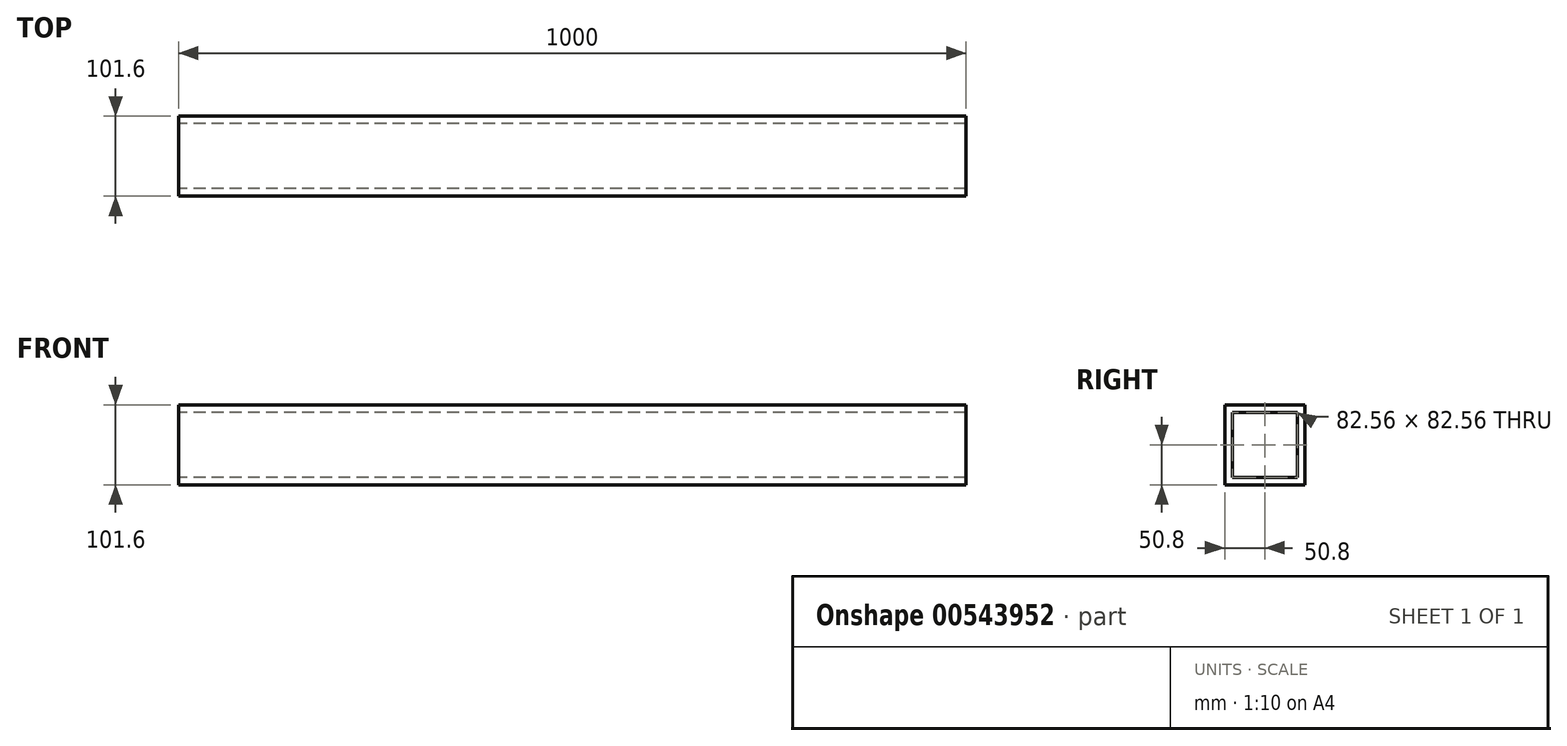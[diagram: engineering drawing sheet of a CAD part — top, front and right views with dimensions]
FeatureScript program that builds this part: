
annotation { "Feature Type Name" : "Feature", "Feature Type Description" : "" }
export const myFeature = defineFeature(function(context is Context, id is Id, definition is map)
    precondition{}
    {
        {
            var Q0;
            Q0=qCreatedBy(makeId("Right.planeOp"),FACE);
            var sketch = newSketch(context, id + "F0", { "sketchPlane" : qUnion([Q0])});
            skLineSegment(sketch, "E0.bottom", {"start": v(-50.8, 50.8) * mm, "end": v(50.8, 50.8) * mm});
            skLineSegment(sketch, "E0.top", {"start": v(-50.8, -50.8) * mm, "end": v(50.8, -50.8) * mm});
            skLineSegment(sketch, "E0.left", {"start": v(-50.8, 50.8) * mm, "end": v(-50.8, -50.8) * mm});
            skLineSegment(sketch, "E0.right", {"start": v(50.8, 50.8) * mm, "end": v(50.8, -50.8) * mm});
            skLineSegment(sketch, "E1.0", {"start": v(-41.28, 41.28) * mm, "end": v(-41.28, -41.28) * mm});
            skLineSegment(sketch, "E1.1", {"start": v(-41.28, 41.28) * mm, "end": v(41.28, 41.28) * mm});
            skLineSegment(sketch, "E1.2", {"start": v(41.28, 41.28) * mm, "end": v(41.28, -41.28) * mm});
            skLineSegment(sketch, "E1.3", {"start": v(-41.28, -41.28) * mm, "end": v(41.28, -41.28) * mm});
            skSolve(sketch);
        }
        {
            var Q0;
            Q0=makeQuery(id+"F0.imprint","IMPRINT",FACE,{"disambiguationData":[TD([[makeQuery(id+"F0.imprint","IMPRINT",EDGE,{"derivedFrom":sQuery(id+"F0.wireOp",EDGE,"E0.bottom")}),-1.0]])]});
            extrude(context, id + "F1", {"entities" : qUnion([Q0]), "depth" : 1000 * mm, "offsetDistance" : 25 * mm});
        }
    });
